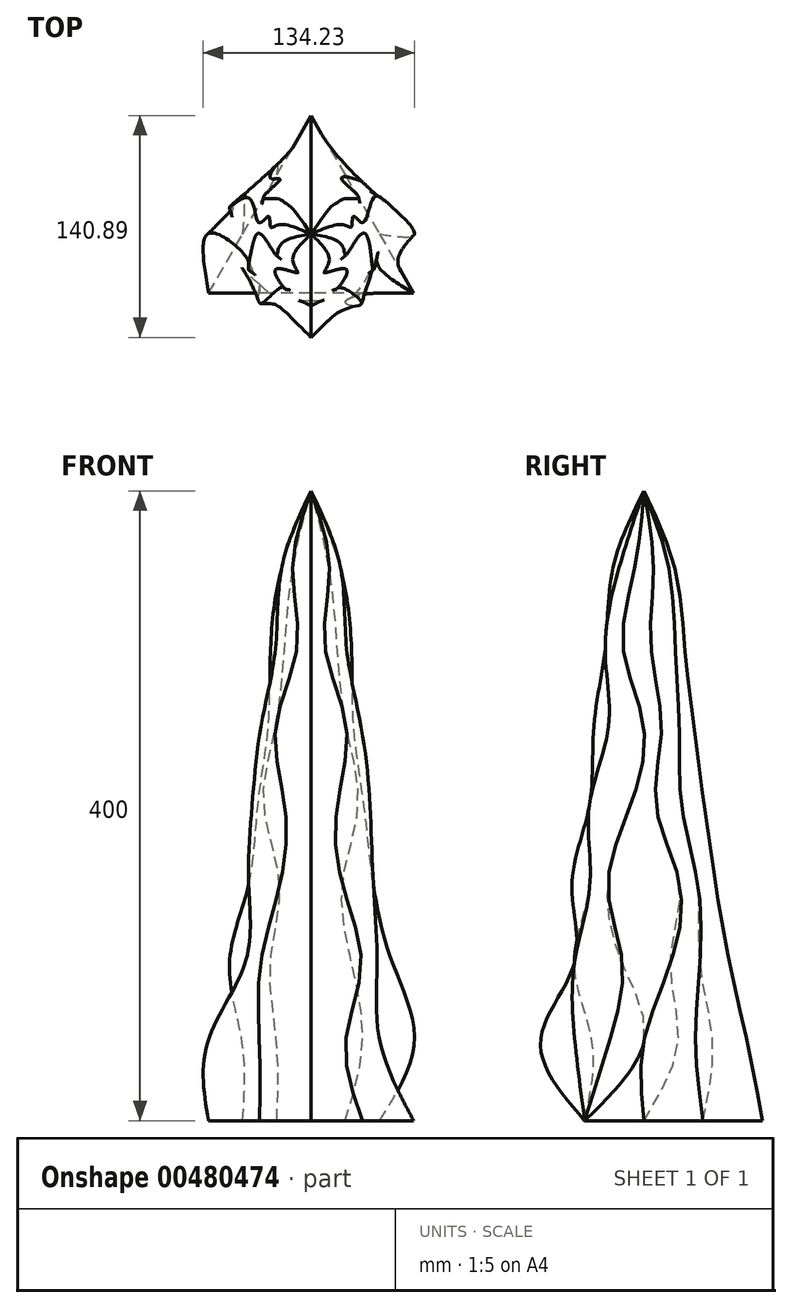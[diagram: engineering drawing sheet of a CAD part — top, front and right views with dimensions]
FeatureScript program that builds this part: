
annotation { "Feature Type Name" : "Feature", "Feature Type Description" : "" }
export const myFeature = defineFeature(function(context is Context, id is Id, definition is map)
    precondition{}
    {
        {
            var Q0;
            Q0=qCreatedBy(makeId("Top.planeOp"),FACE);
            var sketch = newSketch(context, id + "F0", { "sketchPlane" : qUnion([Q0])});
            skCircle(sketch, "E0.cCircle", {"center": v(0, 0) * mm, "radius": 75.22 * mm, "construction": true});
            skLineSegment(sketch, "E0.0", {"start": v(0, 75.22) * mm, "end": v(65.14, -37.6) * mm});
            skLineSegment(sketch, "E0.1", {"start": v(65.14, -37.6) * mm, "end": v(-65.14, -37.6) * mm});
            skLineSegment(sketch, "E0.2", {"start": v(-65.14, -37.6) * mm, "end": v(0, 75.22) * mm});
            skSolve(sketch);
        }
        {
            var Q0;
            Q0=qCreatedBy(makeId("Top.planeOp"),FACE);
            cPlane(context, id + "F1", {"entities" : qUnion([Q0]), "cplaneType" : CPlaneType.OFFSET, "offset" : 50 * mm, "width" : 152.4 * mm, "height" : 152.4 * mm});
        }
        {
            var Q0;
            Q0=qCreatedBy(id+"F1.planeOp",FACE);
            var sketch = newSketch(context, id + "F2", { "sketchPlane" : qUnion([Q0])});
            skCircle(sketch, "E1.cCircle", {"center": v(0, 0) * mm, "radius": 65.63 * mm, "construction": true});
            skLineSegment(sketch, "E1.0", {"start": v(0, 65.63) * mm, "end": v(65.63, 0) * mm});
            skLineSegment(sketch, "E1.1", {"start": v(65.63, 0) * mm, "end": v(0, -65.63) * mm});
            skLineSegment(sketch, "E1.2", {"start": v(0, -65.63) * mm, "end": v(-65.63, 0) * mm});
            skLineSegment(sketch, "E1.3", {"start": v(-65.63, 0) * mm, "end": v(0, 65.63) * mm});
            skSolve(sketch);
        }
        {
            var Q0;
            Q0=qCreatedBy(id+"F1.planeOp",FACE);
            cPlane(context, id + "F3", {"entities" : qUnion([Q0]), "cplaneType" : CPlaneType.OFFSET, "offset" : 50 * mm, "width" : 150 * mm, "height" : 150 * mm});
        }
        {
            var Q0;
            Q0=qCreatedBy(id+"F3.planeOp",FACE);
            var sketch = newSketch(context, id + "F4", { "sketchPlane" : qUnion([Q0])});
            skCircle(sketch, "E2.cCircle", {"center": v(0, 0) * mm, "radius": 54.48 * mm, "construction": true});
            skLineSegment(sketch, "E2.0", {"start": v(0, 54.48) * mm, "end": v(51.82, 16.84) * mm});
            skLineSegment(sketch, "E2.1", {"start": v(51.82, 16.84) * mm, "end": v(32.02, -44.08) * mm});
            skLineSegment(sketch, "E2.2", {"start": v(32.02, -44.08) * mm, "end": v(-32.02, -44.08) * mm});
            skLineSegment(sketch, "E2.3", {"start": v(-32.02, -44.08) * mm, "end": v(-51.82, 16.84) * mm});
            skLineSegment(sketch, "E2.4", {"start": v(-51.82, 16.84) * mm, "end": v(0, 54.48) * mm});
            skSolve(sketch);
        }
        {
            var Q0;
            Q0=qCreatedBy(id+"F3.planeOp",FACE);
            cPlane(context, id + "F5", {"entities" : qUnion([Q0]), "cplaneType" : CPlaneType.OFFSET, "offset" : 50 * mm, "width" : 150 * mm, "height" : 150 * mm});
        }
        {
            var Q0;
            Q0=qCreatedBy(id+"F5.planeOp",FACE);
            var sketch = newSketch(context, id + "F6", { "sketchPlane" : qUnion([Q0])});
            skCircle(sketch, "E3.cCircle", {"center": v(0, 0) * mm, "radius": 45.7 * mm, "construction": true});
            skLineSegment(sketch, "E3.0", {"start": v(0, 45.7) * mm, "end": v(39.58, 22.85) * mm});
            skLineSegment(sketch, "E3.1", {"start": v(39.58, 22.85) * mm, "end": v(39.58, -22.85) * mm});
            skLineSegment(sketch, "E3.2", {"start": v(39.58, -22.85) * mm, "end": v(0, -45.7) * mm});
            skLineSegment(sketch, "E3.3", {"start": v(0, -45.7) * mm, "end": v(-39.58, -22.85) * mm});
            skLineSegment(sketch, "E3.4", {"start": v(-39.58, -22.85) * mm, "end": v(-39.58, 22.85) * mm});
            skLineSegment(sketch, "E3.5", {"start": v(-39.58, 22.85) * mm, "end": v(0, 45.7) * mm});
            skSolve(sketch);
        }
        {
            var Q0;
            Q0=qCreatedBy(id+"F5.planeOp",FACE);
            cPlane(context, id + "F7", {"entities" : qUnion([Q0]), "cplaneType" : CPlaneType.OFFSET, "offset" : 50 * mm, "width" : 150 * mm, "height" : 150 * mm});
        }
        {
            var Q0;
            Q0=qCreatedBy(id+"F7.planeOp",FACE);
            var sketch = newSketch(context, id + "F8", { "sketchPlane" : qUnion([Q0])});
            skCircle(sketch, "E4.cCircle", {"center": v(0, 0) * mm, "radius": 38.43 * mm, "construction": true});
            skLineSegment(sketch, "E4.0", {"start": v(0, 38.43) * mm, "end": v(30.05, 23.96) * mm});
            skLineSegment(sketch, "E4.1", {"start": v(30.05, 23.96) * mm, "end": v(37.47, -8.55) * mm});
            skLineSegment(sketch, "E4.2", {"start": v(37.47, -8.55) * mm, "end": v(16.68, -34.63) * mm});
            skLineSegment(sketch, "E4.3", {"start": v(16.68, -34.63) * mm, "end": v(-16.68, -34.63) * mm});
            skLineSegment(sketch, "E4.4", {"start": v(-16.68, -34.63) * mm, "end": v(-37.47, -8.55) * mm});
            skLineSegment(sketch, "E4.5", {"start": v(-37.47, -8.55) * mm, "end": v(-30.05, 23.96) * mm});
            skLineSegment(sketch, "E4.6", {"start": v(-30.05, 23.96) * mm, "end": v(0, 38.43) * mm});
            skSolve(sketch);
        }
        {
            var Q0;
            Q0=qCreatedBy(id+"F7.planeOp",FACE);
            cPlane(context, id + "F9", {"entities" : qUnion([Q0]), "cplaneType" : CPlaneType.OFFSET, "offset" : 50 * mm, "width" : 150 * mm, "height" : 150 * mm});
        }
        {
            var Q0;
            Q0=qCreatedBy(id+"F9.planeOp",FACE);
            var sketch = newSketch(context, id + "F10", { "sketchPlane" : qUnion([Q0])});
            skCircle(sketch, "E5.cCircle", {"center": v(0, 0) * mm, "radius": 31.84 * mm, "construction": true});
            skLineSegment(sketch, "E5.0", {"start": v(0, 31.84) * mm, "end": v(22.52, 22.52) * mm});
            skLineSegment(sketch, "E5.1", {"start": v(22.52, 22.52) * mm, "end": v(31.84, 0) * mm});
            skLineSegment(sketch, "E5.2", {"start": v(31.84, 0) * mm, "end": v(22.52, -22.52) * mm});
            skLineSegment(sketch, "E5.3", {"start": v(22.52, -22.52) * mm, "end": v(0, -31.84) * mm});
            skLineSegment(sketch, "E5.4", {"start": v(0, -31.84) * mm, "end": v(-22.52, -22.52) * mm});
            skLineSegment(sketch, "E5.5", {"start": v(-22.52, -22.52) * mm, "end": v(-31.84, 0) * mm});
            skLineSegment(sketch, "E5.6", {"start": v(-31.84, 0) * mm, "end": v(-22.52, 22.52) * mm});
            skLineSegment(sketch, "E5.7", {"start": v(-22.52, 22.52) * mm, "end": v(0, 31.84) * mm});
            skSolve(sketch);
        }
        {
            var Q0;
            Q0=qCreatedBy(id+"F9.planeOp",FACE);
            cPlane(context, id + "F11", {"entities" : qUnion([Q0]), "cplaneType" : CPlaneType.OFFSET, "offset" : 50 * mm, "width" : 150 * mm, "height" : 150 * mm});
        }
        {
            var Q0;
            Q0=qCreatedBy(id+"F11.planeOp",FACE);
            var sketch = newSketch(context, id + "F12", { "sketchPlane" : qUnion([Q0])});
            skCircle(sketch, "E6.cCircle", {"center": v(0, 0) * mm, "radius": 26.1 * mm, "construction": true});
            skLineSegment(sketch, "E6.0", {"start": v(0, 26.1) * mm, "end": v(16.78, 20) * mm});
            skLineSegment(sketch, "E6.1", {"start": v(16.78, 20) * mm, "end": v(25.7, 4.53) * mm});
            skLineSegment(sketch, "E6.2", {"start": v(25.7, 4.53) * mm, "end": v(22.6, -13.05) * mm});
            skLineSegment(sketch, "E6.3", {"start": v(22.6, -13.05) * mm, "end": v(8.93, -24.53) * mm});
            skLineSegment(sketch, "E6.4", {"start": v(8.93, -24.53) * mm, "end": v(-8.93, -24.53) * mm});
            skLineSegment(sketch, "E6.5", {"start": v(-8.93, -24.53) * mm, "end": v(-22.6, -13.05) * mm});
            skLineSegment(sketch, "E6.6", {"start": v(-22.6, -13.05) * mm, "end": v(-25.7, 4.53) * mm});
            skLineSegment(sketch, "E6.7", {"start": v(-25.7, 4.53) * mm, "end": v(-16.78, 20) * mm});
            skLineSegment(sketch, "E6.8", {"start": v(-16.78, 20) * mm, "end": v(0, 26.1) * mm});
            skSolve(sketch);
        }
        {
            var Q0;
            Q0=qCreatedBy(id+"F11.planeOp",FACE);
            cPlane(context, id + "F13", {"entities" : qUnion([Q0]), "cplaneType" : CPlaneType.OFFSET, "offset" : 50 * mm, "width" : 150 * mm, "height" : 150 * mm});
        }
        {
            var Q0;
            Q0=qCreatedBy(id+"F13.planeOp",FACE);
            var sketch = newSketch(context, id + "F14", { "sketchPlane" : qUnion([Q0])});
            skCircle(sketch, "E7.cCircle", {"center": v(0, 0) * mm, "radius": 19.85 * mm, "construction": true});
            skLineSegment(sketch, "E7.0", {"start": v(0, 19.85) * mm, "end": v(11.67, 16.06) * mm});
            skLineSegment(sketch, "E7.1", {"start": v(11.67, 16.06) * mm, "end": v(18.88, 6.13) * mm});
            skLineSegment(sketch, "E7.2", {"start": v(18.88, 6.13) * mm, "end": v(18.88, -6.13) * mm});
            skLineSegment(sketch, "E7.3", {"start": v(18.88, -6.13) * mm, "end": v(11.67, -16.06) * mm});
            skLineSegment(sketch, "E7.4", {"start": v(11.67, -16.06) * mm, "end": v(0, -19.85) * mm});
            skLineSegment(sketch, "E7.5", {"start": v(0, -19.85) * mm, "end": v(-11.67, -16.06) * mm});
            skLineSegment(sketch, "E7.6", {"start": v(-11.67, -16.06) * mm, "end": v(-18.88, -6.13) * mm});
            skLineSegment(sketch, "E7.7", {"start": v(-18.88, -6.13) * mm, "end": v(-18.88, 6.13) * mm});
            skLineSegment(sketch, "E7.8", {"start": v(-18.88, 6.13) * mm, "end": v(-11.67, 16.06) * mm});
            skLineSegment(sketch, "E7.9", {"start": v(-11.67, 16.06) * mm, "end": v(0, 19.85) * mm});
            skSolve(sketch);
        }
        {
            var Q0;
            Q0=qCreatedBy(id+"F13.planeOp",FACE);
            cPlane(context, id + "F15", {"entities" : qUnion([Q0]), "cplaneType" : CPlaneType.OFFSET, "offset" : 50 * mm, "width" : 150 * mm, "height" : 150 * mm});
        }
        {
            var Q0;
            Q0=qCreatedBy(id+"F15.planeOp",FACE);
            var sketch = newSketch(context, id + "F16", { "sketchPlane" : qUnion([Q0])});
            skCircle(sketch, "E8", {"center": v(0, 0) * mm, "radius": 13.52 * mm});
            skSolve(sketch);
        }
        {
            var Q0;
            Q0 = qSketchRegion(id + "F0", true);
            var Q1;
            Q1 = qSketchRegion(id + "F2", true);
            var Q2;
            Q2 = qSketchRegion(id + "F4", true);
            var Q3;
            Q3 = qSketchRegion(id + "F6", true);
            var Q4;
            Q4 = qSketchRegion(id + "F8", true);
            var Q5;
            Q5 = qSketchRegion(id + "F10", true);
            var Q6;
            Q6 = qSketchRegion(id + "F12", true);
            var Q7;
            Q7 = qSketchRegion(id + "F14", true);
            var Q8;
            Q8=sQuery(id+"F16.wireOp",VERTEX,"E8.center");
            loft(context, id + "F17", {"sheetProfilesArray" : [{ "sheetProfileEntities" : qUnion([Q0]) }, { "sheetProfileEntities" : qUnion([Q1]) }, { "sheetProfileEntities" : qUnion([Q2]) }, { "sheetProfileEntities" : qUnion([Q3]) }, { "sheetProfileEntities" : qUnion([Q4]) }, { "sheetProfileEntities" : qUnion([Q5]) }, { "sheetProfileEntities" : qUnion([Q6]) }, { "sheetProfileEntities" : qUnion([Q7]) }, { "sheetProfileEntities" : qUnion([Q8]) }]});
        }
    });
